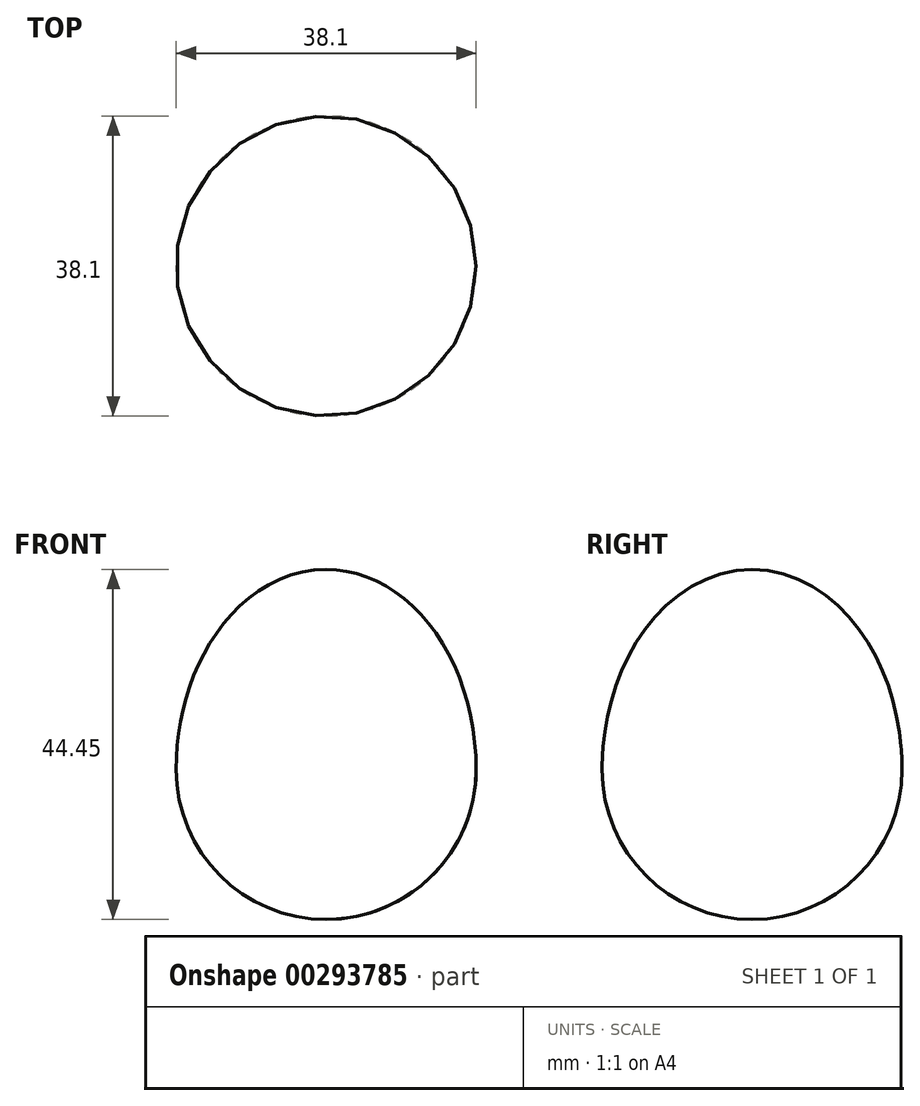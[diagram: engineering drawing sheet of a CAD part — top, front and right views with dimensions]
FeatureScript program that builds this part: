
annotation { "Feature Type Name" : "Feature", "Feature Type Description" : "" }
export const myFeature = defineFeature(function(context is Context, id is Id, definition is map)
    precondition{}
    {
        {
            var Q0;
            Q0=qCreatedBy(makeId("Front.planeOp"),FACE);
            var sketch = newSketch(context, id + "F0", { "sketchPlane" : qUnion([Q0])});
            skArc(sketch, "E0", {"start": v(0, -19.05) * mm, "mid": v(13.47, -13.47) * mm, "end": v(19.05, 0) * mm});
            skEllipticalArc(sketch, "E1", {});
            skLineSegment(sketch, "E2", {"start": v(0, 25.4) * mm, "end": v(0, -19.05) * mm});
            const initialGuessF0  = {"E1": [0, 0, 1, 0, 0.01905, 0.0254, 6.283185307179586, 1.5707963267948966]};
            skSetInitialGuess(sketch, initialGuessF0);
            skSolve(sketch);
        }
        {
            var Q0;
            Q0=makeQuery(id+"F0.imprint","IMPRINT",FACE,{"disambiguationData":[TD([[makeQuery(id+"F0.imprint","IMPRINT",EDGE,{"derivedFrom":sQuery(id+"F0.wireOp",EDGE,"E0")}),1.0]])]});
            var Q1;
            Q1=sQuery(id+"F0.wireOp",EDGE,"E2");
            revolve(context, id + "F1", {"entities" : qUnion([Q0]), "axis" : qUnion([Q1]), "revolveType" : RevolveType.FULL});
        }
    });
